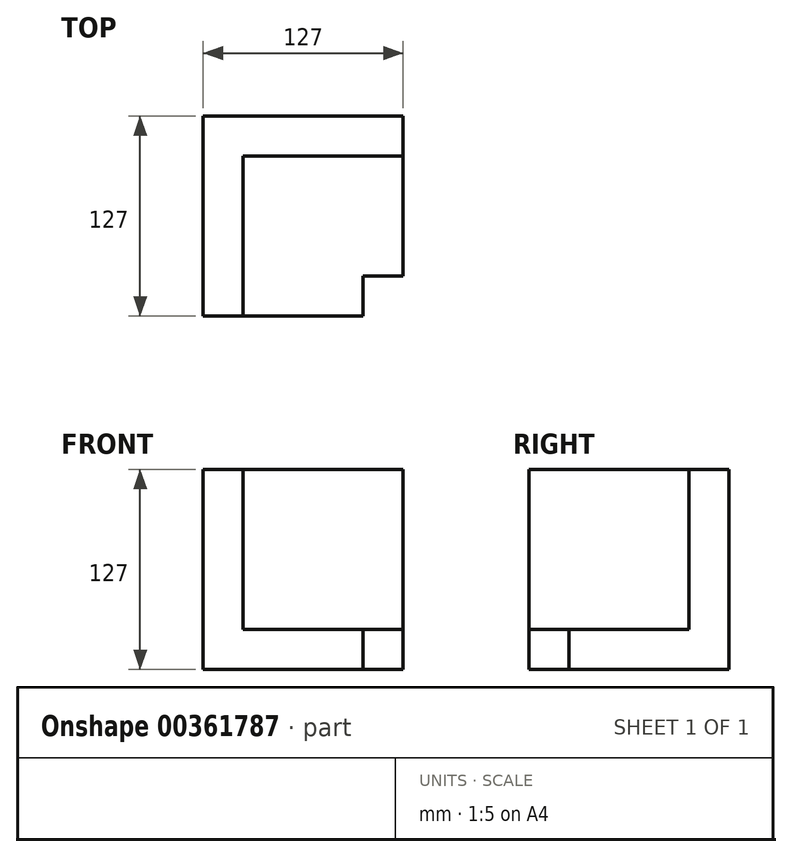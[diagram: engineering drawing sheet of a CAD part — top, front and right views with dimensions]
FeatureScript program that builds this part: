
annotation { "Feature Type Name" : "Feature", "Feature Type Description" : "" }
export const myFeature = defineFeature(function(context is Context, id is Id, definition is map)
    precondition{}
    {
        {
            var Q0;
            Q0=qCreatedBy(makeId("Top.planeOp"),FACE);
            var sketch = newSketch(context, id + "F0", { "sketchPlane" : qUnion([Q0])});
            skLineSegment(sketch, "E0.bottom", {"start": v(-56.39, 59.87) * mm, "end": v(70.61, 59.87) * mm});
            skLineSegment(sketch, "E0.top", {"start": v(-56.39, -67.13) * mm, "end": v(70.61, -67.13) * mm});
            skLineSegment(sketch, "E0.left", {"start": v(-56.39, 59.87) * mm, "end": v(-56.39, -67.13) * mm});
            skLineSegment(sketch, "E0.right", {"start": v(70.61, 59.87) * mm, "end": v(70.61, -67.13) * mm});
            skSolve(sketch);
        }
        {
            var Q0;
            Q0=makeQuery(id+"F0.imprint","IMPRINT",FACE,{"disambiguationData":[TD([[makeQuery(id+"F0.imprint","IMPRINT",EDGE,{"derivedFrom":sQuery(id+"F0.wireOp",EDGE,"E0.bottom")}),-1.0]])]});
            extrude(context, id + "F1", {"entities" : qUnion([Q0]), "depth" : 25.4 * mm});
        }
        {
            var Q0;
            Q0=makeQuery(id+"F1.opExtrude","CAP_FACE",FACE,{"disambiguationData":[OSD([sQuery(id+"F0.wireOp",EDGE,"E0.bottom"),sQuery(id+"F0.wireOp",EDGE,"E0.top"),sQuery(id+"F0.wireOp",EDGE,"E0.left"),sQuery(id+"F0.wireOp",EDGE,"E0.right")])],"isStart":false});
            var sketch = newSketch(context, id + "F2", { "sketchPlane" : qUnion([Q0])});
            skLineSegment(sketch, "E1.bottom", {"start": v(-56.39, 59.87) * mm, "end": v(-30.99, 59.87) * mm});
            skLineSegment(sketch, "E1.top", {"start": v(-56.39, -67.13) * mm, "end": v(-30.99, -67.13) * mm});
            skLineSegment(sketch, "E1.left", {"start": v(-56.39, 59.87) * mm, "end": v(-56.39, -67.13) * mm});
            skLineSegment(sketch, "E1.right", {"start": v(-30.99, 59.87) * mm, "end": v(-30.99, -67.13) * mm});
            skSolve(sketch);
        }
        {
            var Q0;
            Q0 = qSketchRegion(id + "F2", true);
            var Q1;
            Q1=makeQuery(id+"F2.imprint","IMPRINT",FACE,{"disambiguationData":[TD([[makeQuery(id+"F2.imprint","IMPRINT",EDGE,{"derivedFrom":sQuery(id+"F2.wireOp",EDGE,"E1.bottom")}),-1.0]])]});
            extrude(context, id + "F3", {"entities" : qUnion([Q0, Q1]), "operationType" : NewBodyOperationType.ADD, "depth" : 101.6 * mm});
        }
        {
            var Q0;
            Q0=makeQuery(id+"F1.opExtrude","CAP_FACE",FACE,{"disambiguationData":[OSD([sQuery(id+"F0.wireOp",EDGE,"E0.bottom"),sQuery(id+"F0.wireOp",EDGE,"E0.top"),sQuery(id+"F0.wireOp",EDGE,"E0.left"),sQuery(id+"F0.wireOp",EDGE,"E0.right")])],"isStart":false});
            var sketch = newSketch(context, id + "F4", { "sketchPlane" : qUnion([Q0])});
            skLineSegment(sketch, "E2.bottom", {"start": v(-30.99, 59.87) * mm, "end": v(70.61, 59.87) * mm});
            skLineSegment(sketch, "E2.top", {"start": v(-30.99, 34.47) * mm, "end": v(70.61, 34.47) * mm});
            skLineSegment(sketch, "E2.left", {"start": v(-30.99, 59.87) * mm, "end": v(-30.99, 34.47) * mm});
            skLineSegment(sketch, "E2.right", {"start": v(70.61, 59.87) * mm, "end": v(70.61, 34.47) * mm});
            skSolve(sketch);
        }
        {
            var Q0;
            Q0=makeQuery(id+"F4.imprint","IMPRINT",FACE,{"disambiguationData":[TD([[makeQuery(id+"F4.imprint","IMPRINT",EDGE,{"derivedFrom":sQuery(id+"F4.wireOp",EDGE,"E2.bottom")}),-1.0]])]});
            extrude(context, id + "F5", {"entities" : qUnion([Q0]), "operationType" : NewBodyOperationType.ADD, "depth" : 101.6 * mm});
        }
        {
            var Q0;
            Q0=makeQuery(id+"F1.opExtrude","CAP_FACE",FACE,{"disambiguationData":[OSD([sQuery(id+"F0.wireOp",EDGE,"E0.bottom"),sQuery(id+"F0.wireOp",EDGE,"E0.top"),sQuery(id+"F0.wireOp",EDGE,"E0.left"),sQuery(id+"F0.wireOp",EDGE,"E0.right")])],"isStart":false});
            var sketch = newSketch(context, id + "F6", { "sketchPlane" : qUnion([Q0])});
            skLineSegment(sketch, "E3.bottom", {"start": v(70.61, -67.13) * mm, "end": v(45.21, -67.13) * mm});
            skLineSegment(sketch, "E3.top", {"start": v(70.61, -41.73) * mm, "end": v(45.21, -41.73) * mm});
            skLineSegment(sketch, "E3.left", {"start": v(70.61, -67.13) * mm, "end": v(70.61, -41.73) * mm});
            skLineSegment(sketch, "E3.right", {"start": v(45.21, -67.13) * mm, "end": v(45.21, -41.73) * mm});
            skSolve(sketch);
        }
        {
            var Q0;
            Q0=makeQuery(id+"F6.imprint","IMPRINT",FACE,{"disambiguationData":[TD([[makeQuery(id+"F6.imprint","IMPRINT",EDGE,{"derivedFrom":sQuery(id+"F6.wireOp",EDGE,"E3.bottom")}),1.0]])]});
            extrude(context, id + "F7", {"entities" : qUnion([Q0]), "operationType" : NewBodyOperationType.REMOVE, "oppositeDirection" : true, "depth" : 25.4 * mm});
        }
    });
